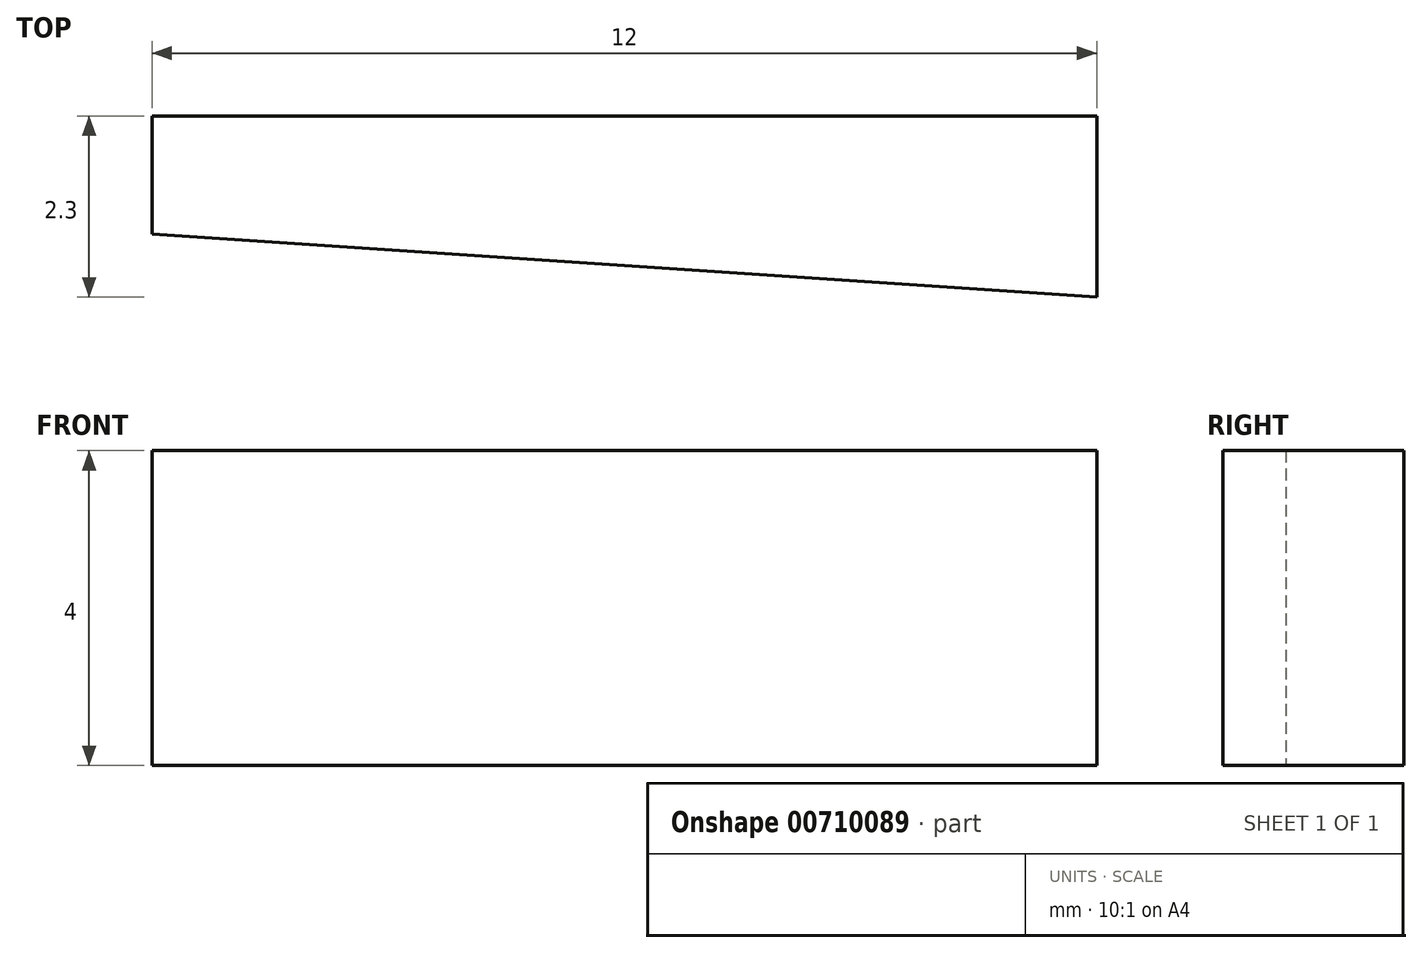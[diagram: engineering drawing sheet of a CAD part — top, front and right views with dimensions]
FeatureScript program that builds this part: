
annotation { "Feature Type Name" : "Feature", "Feature Type Description" : "" }
export const myFeature = defineFeature(function(context is Context, id is Id, definition is map)
    precondition{}
    {
        {
            var Q0;
            Q0=qCreatedBy(makeId("Top.planeOp"),FACE);
            var sketch = newSketch(context, id + "F0", { "sketchPlane" : qUnion([Q0])});
            skLineSegment(sketch, "E0", {"start": v(0, 0) * mm, "end": v(0, -1.5) * mm});
            skLineSegment(sketch, "E1", {"start": v(0, -1.5) * mm, "end": v(12, -2.3) * mm});
            skLineSegment(sketch, "E2", {"start": v(12, -2.3) * mm, "end": v(12, 0) * mm});
            skLineSegment(sketch, "E3", {"start": v(12, 0) * mm, "end": v(0, 0) * mm});
            skSolve(sketch);
        }
        {
            var Q0;
            Q0=makeQuery(id+"F0.imprint","IMPRINT",FACE,{"disambiguationData":[TD([[makeQuery(id+"F0.imprint","IMPRINT",EDGE,{"derivedFrom":sQuery(id+"F0.wireOp",EDGE,"E0")}),1.0]])]});
            extrude(context, id + "F1", {"entities" : qUnion([Q0]), "depth" : 4 * mm, "offsetDistance" : 25 * mm});
        }
    });
